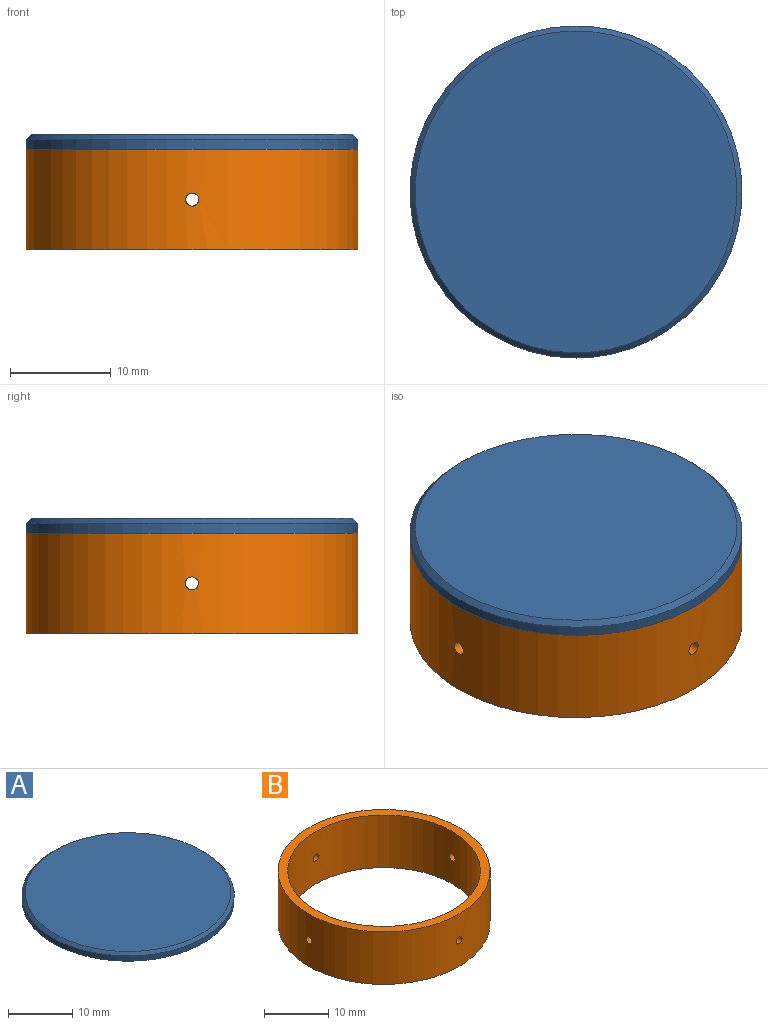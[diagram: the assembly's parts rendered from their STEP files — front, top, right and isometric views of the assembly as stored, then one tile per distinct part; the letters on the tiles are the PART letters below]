
ASSEMBLY  parts=2 mates=1
PART A: 4 faces, bbox 33x33x1.5 mm
  f0: cylinder r=16.5mm len=33mm, axis (0,0,-1), area 103.7mm2, adj f2,f3
  f1: plane 32x32mm, normal (0,0,1), area 804.2mm2, adj f3
  f2: plane 33x33mm, normal (0,0,-1), area 855.3mm2, adj f0
  f3: cone r=16mm half-angle=45deg, axis (0,0,-1), area 72.2mm2, adj f0,f1
PART B: 8 faces, bbox 33x33x10 mm
  f0: cylinder r=15mm len=30mm, axis (0,0,-1), area 937.2mm2, adj f2,f3,f4,f5,f6,f7
  f1: cylinder r=16.5mm len=33mm, axis (0,0,-1), area 1031.4mm2, adj f2,f3,f4,f5,f6,f7
  f2: plane 33x33mm, normal (0,0,1), area 148.4mm2, adj f0,f1
  f3: plane 33x33mm, normal (0,0,-1), area 148.4mm2, adj f0,f1
  f4: cylinder r=0.65mm len=1.51mm, axis (1,0,0), area 6.1mm2, adj f0,f1
  f5: cylinder r=0.65mm len=1.51mm, axis (1,0,0), area 6.1mm2, adj f0,f1
  f6: cylinder r=0.65mm len=1.52mm, axis (0,-1,0), area 6.1mm2, adj f0,f1
  f7: cylinder r=0.65mm len=1.52mm, axis (0,-1,0), area 6.1mm2, adj f0,f1
PLACE A rot(axis=(0,1,0),0deg) t=(-54.87,110.63,-23.44)mm
PLACE B rot(axis=(0,1,0),0deg) t=(-54.87,110.63,-33.44)mm
MATE fastened B.f1 <-> A.f0  axis (0,0,1) through (-54.87,110.63,-23.44)mm
